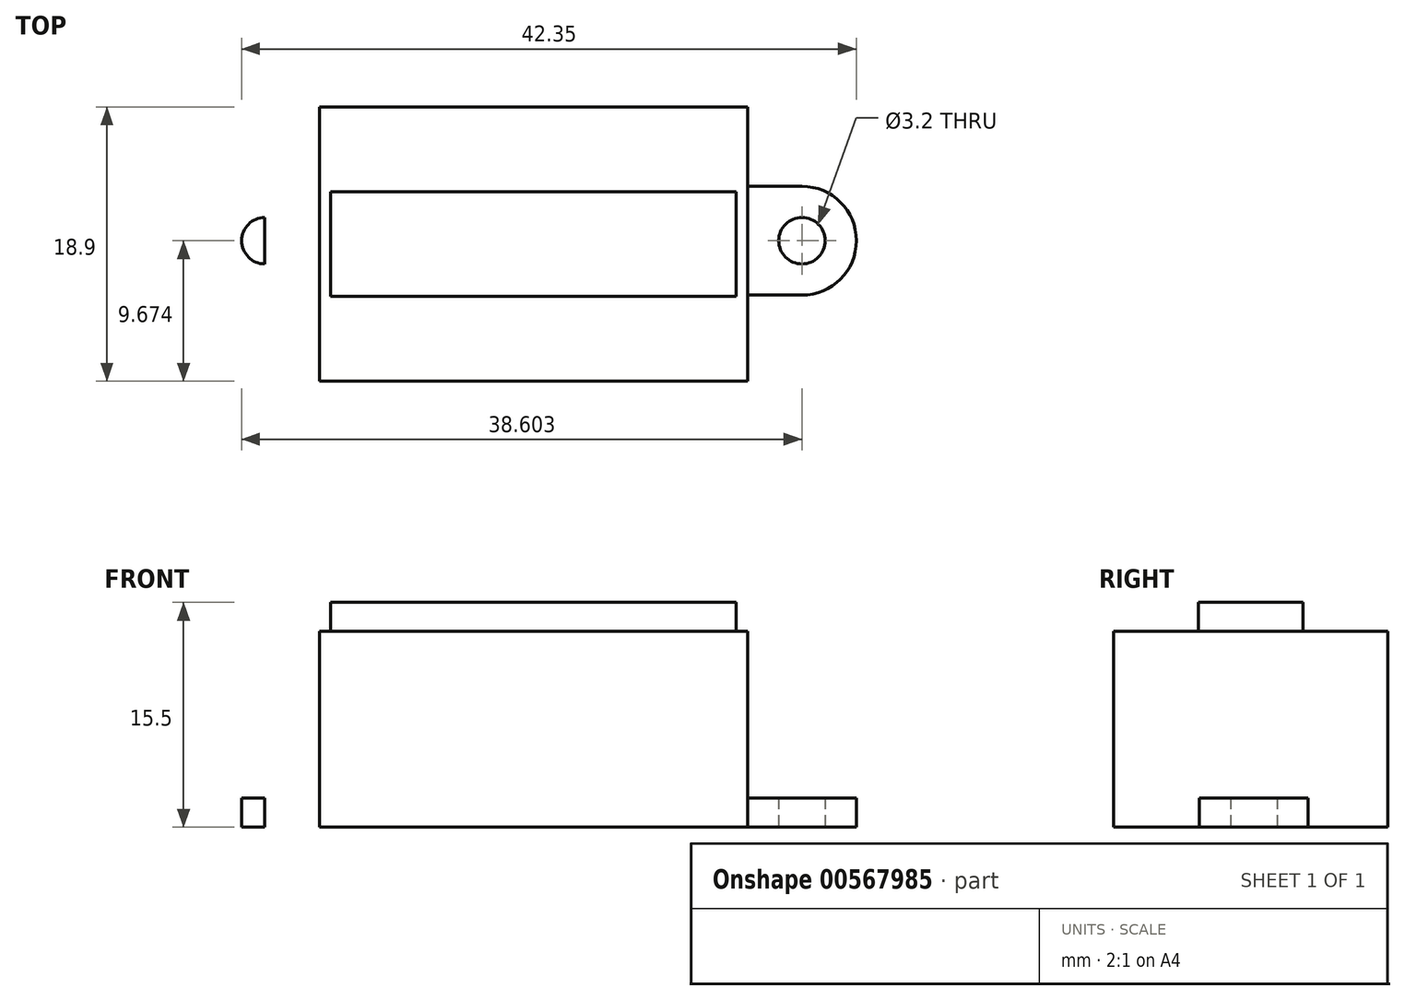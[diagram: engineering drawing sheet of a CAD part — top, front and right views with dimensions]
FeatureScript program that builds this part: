
annotation { "Feature Type Name" : "Feature", "Feature Type Description" : "" }
export const myFeature = defineFeature(function(context is Context, id is Id, definition is map)
    precondition{}
    {
        {
            var Q0;
            Q0=qCreatedBy(makeId("Top.planeOp"),FACE);
            var sketch = newSketch(context, id + "F0", { "sketchPlane" : qUnion([Q0])});
            skLineSegment(sketch, "E0.bottom", {"start": v(-17.08, -18.4) * mm, "end": v(12.42, -18.4) * mm});
            skLineSegment(sketch, "E0.top", {"start": v(-17.08, 0.5) * mm, "end": v(12.42, 0.5) * mm});
            skLineSegment(sketch, "E0.left", {"start": v(-17.08, -18.4) * mm, "end": v(-17.08, 0.5) * mm});
            skLineSegment(sketch, "E0.right", {"start": v(12.42, -18.4) * mm, "end": v(12.42, 0.5) * mm});
            skSolve(sketch);
        }
        {
            var Q0;
            Q0=makeQuery(id+"F0.imprint","IMPRINT",FACE,{"disambiguationData":[TD([[makeQuery(id+"F0.imprint","IMPRINT",EDGE,{"derivedFrom":sQuery(id+"F0.wireOp",EDGE,"E0.bottom")}),1.0]])]});
            extrude(context, id + "F1", {"entities" : qUnion([Q0]), "depth" : 13.5 * mm, "offsetDistance" : 25 * mm});
        }
        {
            var Q0;
            Q0=makeQuery(id+"F1.opExtrude","CAP_FACE",FACE,{"disambiguationData":[OSD([sQuery(id+"F0.wireOp",EDGE,"E0.bottom"),sQuery(id+"F0.wireOp",EDGE,"E0.top"),sQuery(id+"F0.wireOp",EDGE,"E0.left"),sQuery(id+"F0.wireOp",EDGE,"E0.right")])],"isStart":true});
            var sketch = newSketch(context, id + "F2", { "sketchPlane" : qUnion([Q0])});
            skLineSegment(sketch, "E1.bottom", {"start": v(-20.83, 4.98) * mm, "end": v(16.17, 4.98) * mm});
            skLineSegment(sketch, "E1.top", {"start": v(-20.83, 12.48) * mm, "end": v(16.17, 12.48) * mm});
            skLineSegment(sketch, "E1.left", {"start": v(-20.83, 4.98) * mm, "end": v(-20.83, 12.48) * mm});
            skLineSegment(sketch, "E1.right", {"start": v(16.17, 4.98) * mm, "end": v(16.17, 12.48) * mm, "construction": true});
            skLineSegment(sketch, "E2", {"start": v(16.17, 8.73) * mm, "end": v(12.42, 8.73) * mm, "construction": true});
            skPoint(sketch, "E2.endSnap0", {"position": v(12.42, 8.95) * mm});
            skLineSegment(sketch, "E3", {"start": v(-2.33, 12.48) * mm, "end": v(-2.33, 18.4) * mm, "construction": true});
            skArc(sketch, "E4", {"start": v(16.17, 4.98) * mm, "mid": v(19.92, 8.73) * mm, "end": v(16.17, 12.48) * mm});
            skCircle(sketch, "E5", {"center": v(16.17, 8.73) * mm, "radius": 1.6 * mm});
            skArc(sketch, "E6.MirrorCS", {"start": v(-20.83, 4.98) * mm, "mid": v(-24.58, 8.73) * mm, "end": v(-20.83, 12.48) * mm});
            skCircle(sketch, "E7.MirrorC", {"center": v(-20.83, 8.73) * mm, "radius": 1.6 * mm});
            skLineSegment(sketch, "E8.MirrorCS", {"start": v(-20.83, 4.98) * mm, "end": v(-20.83, 12.48) * mm, "construction": true});
            skLineSegment(sketch, "E9.MirrorCS", {"start": v(-20.83, 8.73) * mm, "end": v(-17.08, 8.73) * mm, "construction": true});
            skSolve(sketch);
        }
        {
            var Q0;
            {var subQ1=sQuery(id+"F2.wireOp",EDGE,"E1.left");var subQ4=sQuery(id+"F2.wireOp",EDGE,"E7.MirrorC");var subQ5=makeQuery(id+"F2.imprint","INTERSECT",VERTEX,{"disambiguationData":[OD(0.0)],"derivedFrom":[subQ1,subQ4]});Q0=makeQuery(id+"F2.imprint","IMPRINT",FACE,{"disambiguationData":[TD([[makeQuery(id+"F2.imprint","IMPRINT",EDGE,{"disambiguationData":[TD([[subQ5,1.0]])],"derivedFrom":subQ4}),1.0]])]});}
            var Q1;
            {var subQ0=sQuery(id+"F2.wireOp",EDGE,"E6.MirrorCS");Q1=makeQuery(id+"F2.imprint","IMPRINT",FACE,{"disambiguationData":[TD([[makeQuery(id+"F2.imprint","IMPRINT",EDGE,{"derivedFrom":subQ0}),-1.0]])]});}
            var Q2;
            {var subQ0=sQuery(id+"F2.wireOp",EDGE,"E4");Q2=makeQuery(id+"F2.imprint","IMPRINT",FACE,{"disambiguationData":[TD([[makeQuery(id+"F2.imprint","IMPRINT",EDGE,{"derivedFrom":subQ0}),1.0]])]});}
            extrude(context, id + "F3", {"entities" : qUnion([Q0, Q1, Q2]), "operationType" : NewBodyOperationType.ADD, "oppositeDirection" : true, "depth" : 2 * mm, "offsetDistance" : 25 * mm});
        }
        {
            var Q0;
            Q0=makeQuery(id+"F1.opExtrude","CAP_FACE",FACE,{"disambiguationData":[OSD([sQuery(id+"F0.wireOp",EDGE,"E0.bottom"),sQuery(id+"F0.wireOp",EDGE,"E0.top"),sQuery(id+"F0.wireOp",EDGE,"E0.left"),sQuery(id+"F0.wireOp",EDGE,"E0.right")])],"isStart":false});
            var sketch = newSketch(context, id + "F4", { "sketchPlane" : qUnion([Q0])});
            skLineSegment(sketch, "E10.bottom", {"start": v(-16.3, -5.35) * mm, "end": v(11.65, -5.35) * mm});
            skLineSegment(sketch, "E10.top", {"start": v(-16.3, -12.55) * mm, "end": v(11.65, -12.55) * mm});
            skLineSegment(sketch, "E10.left", {"start": v(-16.3, -5.35) * mm, "end": v(-16.3, -12.55) * mm});
            skLineSegment(sketch, "E10.right", {"start": v(11.65, -5.35) * mm, "end": v(11.65, -12.55) * mm});
            skLineSegment(sketch, "E11", {"start": v(12.42, -8.95) * mm, "end": v(11.65, -8.95) * mm, "construction": true});
            skLineSegment(sketch, "E12", {"start": v(-2.33, 0.5) * mm, "end": v(-2.33, -5.35) * mm, "construction": true});
            skSolve(sketch);
        }
        {
            var Q0;
            Q0=makeQuery(id+"F4.imprint","IMPRINT",FACE,{"disambiguationData":[TD([[makeQuery(id+"F4.imprint","IMPRINT",EDGE,{"derivedFrom":sQuery(id+"F4.wireOp",EDGE,"E10.bottom")}),-1.0]])]});
            extrude(context, id + "F5", {"entities" : qUnion([Q0]), "operationType" : NewBodyOperationType.ADD, "depth" : 2 * mm, "offsetDistance" : 25 * mm});
        }
    });
